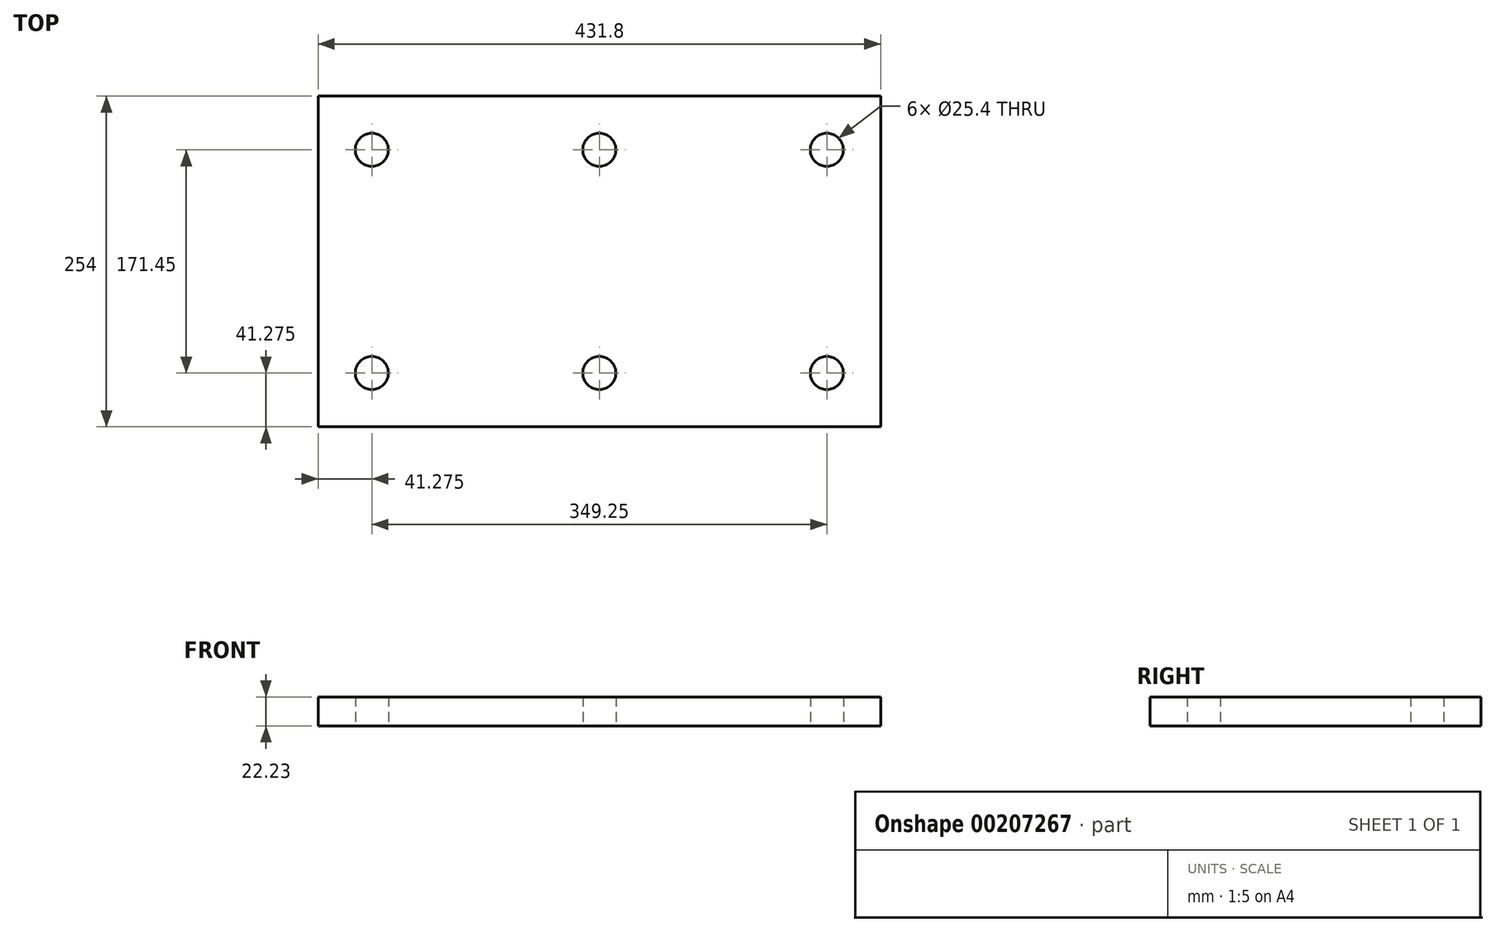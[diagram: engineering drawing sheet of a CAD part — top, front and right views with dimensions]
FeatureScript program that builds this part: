
annotation { "Feature Type Name" : "Feature", "Feature Type Description" : "" }
export const myFeature = defineFeature(function(context is Context, id is Id, definition is map)
    precondition{}
    {
        {
            var Q0;
            Q0=qCreatedBy(makeId("Top.planeOp"),FACE);
            var sketch = newSketch(context, id + "F0", { "sketchPlane" : qUnion([Q0])});
            skLineSegment(sketch, "E0.bottom", {"start": v(-215.9, 127) * mm, "end": v(215.9, 127) * mm});
            skLineSegment(sketch, "E0.top", {"start": v(-215.9, -127) * mm, "end": v(215.9, -127) * mm});
            skLineSegment(sketch, "E0.left", {"start": v(-215.9, 127) * mm, "end": v(-215.9, -127) * mm});
            skLineSegment(sketch, "E0.right", {"start": v(215.9, 127) * mm, "end": v(215.9, -127) * mm});
            skPoint(sketch, "E0.middle", {"position": v(0, 0) * mm});
            skCircle(sketch, "E1", {"center": v(-174.63, 85.72) * mm, "radius": 12.7 * mm});
            skCircle(sketch, "E2", {"center": v(0, 85.72) * mm, "radius": 12.7 * mm});
            skCircle(sketch, "E3", {"center": v(174.62, 85.72) * mm, "radius": 12.7 * mm});
            skCircle(sketch, "E4", {"center": v(174.62, -85.72) * mm, "radius": 12.7 * mm});
            skCircle(sketch, "E5", {"center": v(0, -85.72) * mm, "radius": 12.7 * mm});
            skCircle(sketch, "E6", {"center": v(-174.63, -85.72) * mm, "radius": 12.7 * mm});
            skSolve(sketch);
        }
        {
            var Q0;
            Q0=makeQuery(id+"F0.imprint","IMPRINT",FACE,{"disambiguationData":[TD([[makeQuery(id+"F0.imprint","IMPRINT",EDGE,{"derivedFrom":sQuery(id+"F0.wireOp",EDGE,"E0.bottom")}),-1.0]])]});
            extrude(context, id + "F1", {"entities" : qUnion([Q0]), "depth" : 22.22 * mm});
        }
    });
